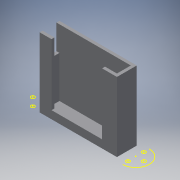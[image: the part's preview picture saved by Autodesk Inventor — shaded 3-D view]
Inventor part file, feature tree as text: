
AUTODESK INVENTOR PART (.ipt)
format: ipt  version: 2016 (Build 200138000, 138)  size: 169,472 bytes
history: native  units: mm
features: extrude x6, sketch x6, fillet x1, projected_geometry x1
ambient origin geometry x8: Origin, YZ Plane, XZ Plane, XY Plane, X Axis, Y Axis, Z Axis, Center Point
bodies: Solid1 (feature_tree)
feature tree (14):
  extrude  "Extrusion1"  Depth=72.0mm
  extrude  "Extrusion2"  Depth=78.0mm
  extrude  "Extrusion3"  Depth=78.0mm
  extrude  "Extrusion4"  Depth=10.0mm TaperAngle=0.0deg
  extrude  "Extrusion5"  Depth=3.0mm TaperAngle=0.0deg
  extrude  "Extrusion6"  Depth=20.0mm TaperAngle=0.0deg
  fillet  "Fillet1"  Radius=5.0mm
  sketch  "Sketch1"  dims[d0=14.0mm d1=72.0mm]
  sketch  "Sketch2"  dims[d2=20.0mm d3=78.0mm]
  sketch  "Sketch3"  dims[d4=42.0mm d5=0.0mm d6=78.0mm]
  sketch  "Sketch4"  dims[d7=51.0mm d9=10.0mm d10=0.0mm]
  sketch  "Sketch5"  dims[d11=25.0mm d12=0.0mm d13=3.0mm d14=0.0mm]
  sketch  "Sketch6"  dims[d15=3.0mm d16=0.0mm d17=20.0mm d18=0.0mm d19=5.0mm]
  projected_geometry  "Projected Loop1"
